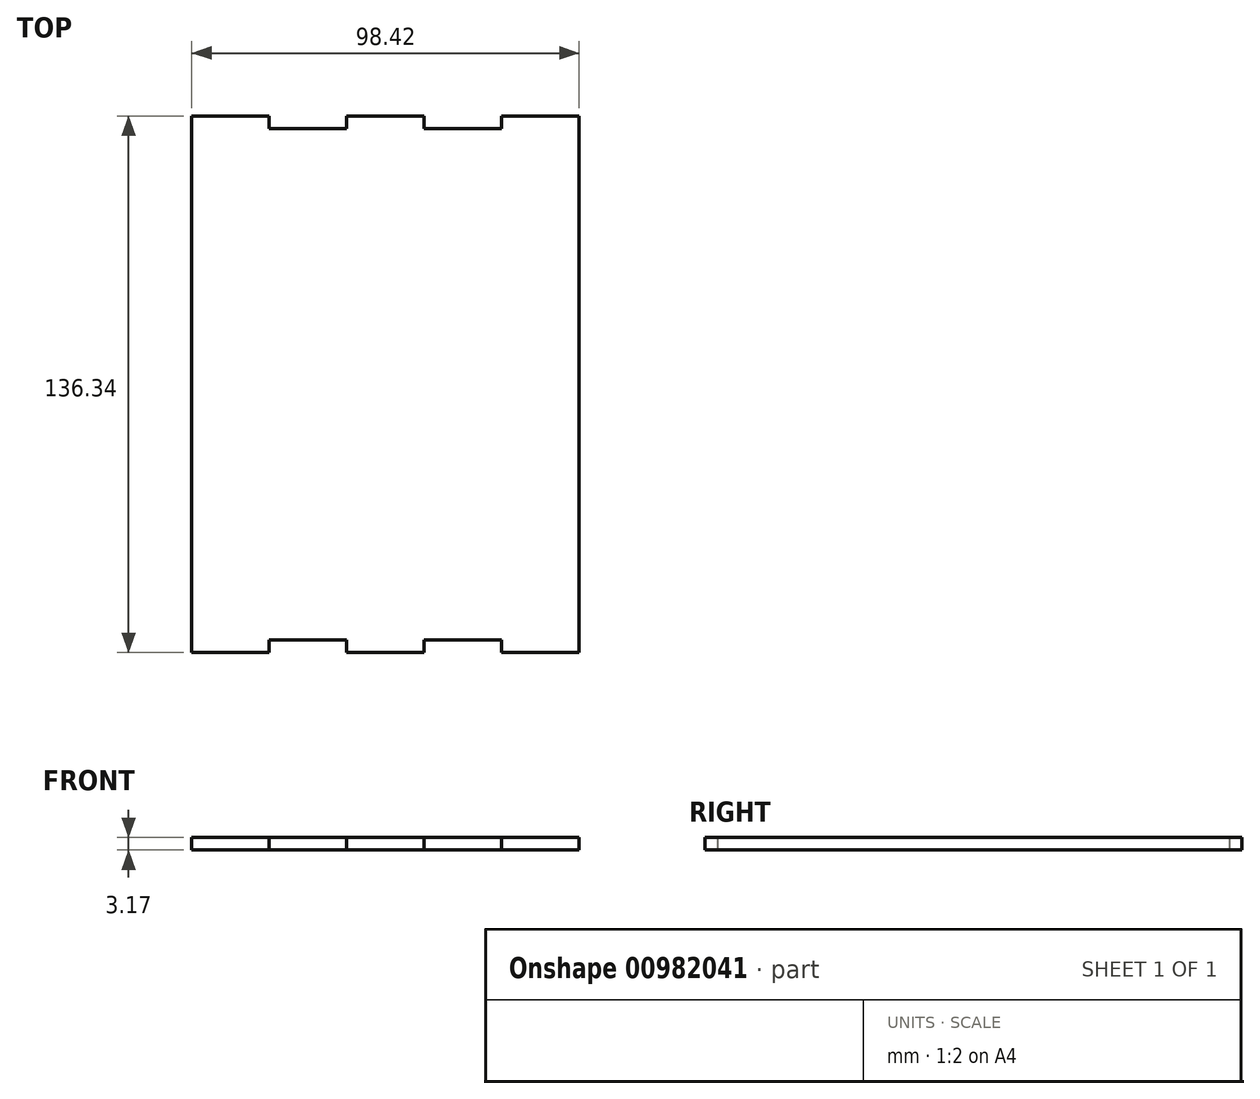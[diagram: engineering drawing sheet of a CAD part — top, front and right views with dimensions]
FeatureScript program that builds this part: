
annotation { "Feature Type Name" : "Feature", "Feature Type Description" : "" }
export const myFeature = defineFeature(function(context is Context, id is Id, definition is map)
    precondition{}
    {
        {
            var Q0;
            Q0=qCreatedBy(makeId("Top.planeOp"),FACE);
            var sketch = newSketch(context, id + "F0", { "sketchPlane" : qUnion([Q0])});
            skLineSegment(sketch, "E0.bottom", {"start": v(49.21, -65) * mm, "end": v(-49.21, -65) * mm, "construction": true});
            skLineSegment(sketch, "E0.top", {"start": v(49.21, 65) * mm, "end": v(-49.21, 65) * mm, "construction": true});
            skLineSegment(sketch, "E0.left", {"start": v(49.21, -65) * mm, "end": v(49.21, 65) * mm});
            skLineSegment(sketch, "E0.right", {"start": v(-49.21, -65) * mm, "end": v(-49.21, 65) * mm});
            skPoint(sketch, "E0.middle", {"position": v(0, 0) * mm});
            skLineSegment(sketch, "E1.top", {"start": v(-49.21, 68.17) * mm, "end": v(-29.53, 68.17) * mm});
            skLineSegment(sketch, "E1.left", {"start": v(-49.21, 65) * mm, "end": v(-49.21, 68.17) * mm});
            skLineSegment(sketch, "E1.right", {"start": v(-29.53, 65) * mm, "end": v(-29.53, 68.17) * mm});
            skLineSegment(sketch, "E2.top", {"start": v(49.21, 68.18) * mm, "end": v(29.53, 68.17) * mm});
            skLineSegment(sketch, "E2.left", {"start": v(49.21, 65) * mm, "end": v(49.21, 68.18) * mm});
            skLineSegment(sketch, "E2.right", {"start": v(29.53, 65) * mm, "end": v(29.53, 68.18) * mm});
            skLineSegment(sketch, "E3.top", {"start": v(-9.84, 68.18) * mm, "end": v(9.84, 68.18) * mm});
            skLineSegment(sketch, "E3.left", {"start": v(-9.84, 65) * mm, "end": v(-9.84, 68.18) * mm});
            skLineSegment(sketch, "E3.right", {"start": v(9.84, 65) * mm, "end": v(9.84, 68.18) * mm});
            skLineSegment(sketch, "E4", {"start": v(-29.53, 65) * mm, "end": v(-9.84, 65) * mm});
            skLineSegment(sketch, "E5", {"start": v(9.84, 65) * mm, "end": v(29.53, 65) * mm});
            skLineSegment(sketch, "E6.MirrorCS", {"start": v(-49.21, -65) * mm, "end": v(-49.21, -68.17) * mm});
            skLineSegment(sketch, "E7.MirrorCS", {"start": v(29.53, -65) * mm, "end": v(29.53, -68.18) * mm});
            skLineSegment(sketch, "E8.MirrorCS", {"start": v(-9.84, -65) * mm, "end": v(-9.84, -68.18) * mm});
            skLineSegment(sketch, "E9.MirrorCS", {"start": v(-29.53, -65) * mm, "end": v(-29.53, -68.17) * mm});
            skLineSegment(sketch, "E10.MirrorCS", {"start": v(9.84, -65) * mm, "end": v(9.84, -68.18) * mm});
            skLineSegment(sketch, "E11.MirrorCS", {"start": v(49.21, -65) * mm, "end": v(49.21, -68.18) * mm});
            skLineSegment(sketch, "E12.MirrorCS", {"start": v(9.84, -65) * mm, "end": v(29.53, -65) * mm});
            skLineSegment(sketch, "E13.MirrorCS", {"start": v(-29.53, -65) * mm, "end": v(-9.84, -65) * mm});
            skLineSegment(sketch, "E14.MirrorCS", {"start": v(49.21, -68.18) * mm, "end": v(29.53, -68.17) * mm});
            skLineSegment(sketch, "E15.MirrorCS", {"start": v(-49.21, -68.17) * mm, "end": v(-29.53, -68.17) * mm});
            skLineSegment(sketch, "E16.MirrorCS", {"start": v(-9.84, -68.18) * mm, "end": v(9.84, -68.18) * mm});
            skSolve(sketch);
        }
        {
            var Q0;
            Q0 = qSketchRegion(id + "F0", true);
            extrude(context, id + "F1", {"entities" : qUnion([Q0]), "depth" : 3.17 * mm, "offsetDistance" : 25 * mm});
        }
    });
